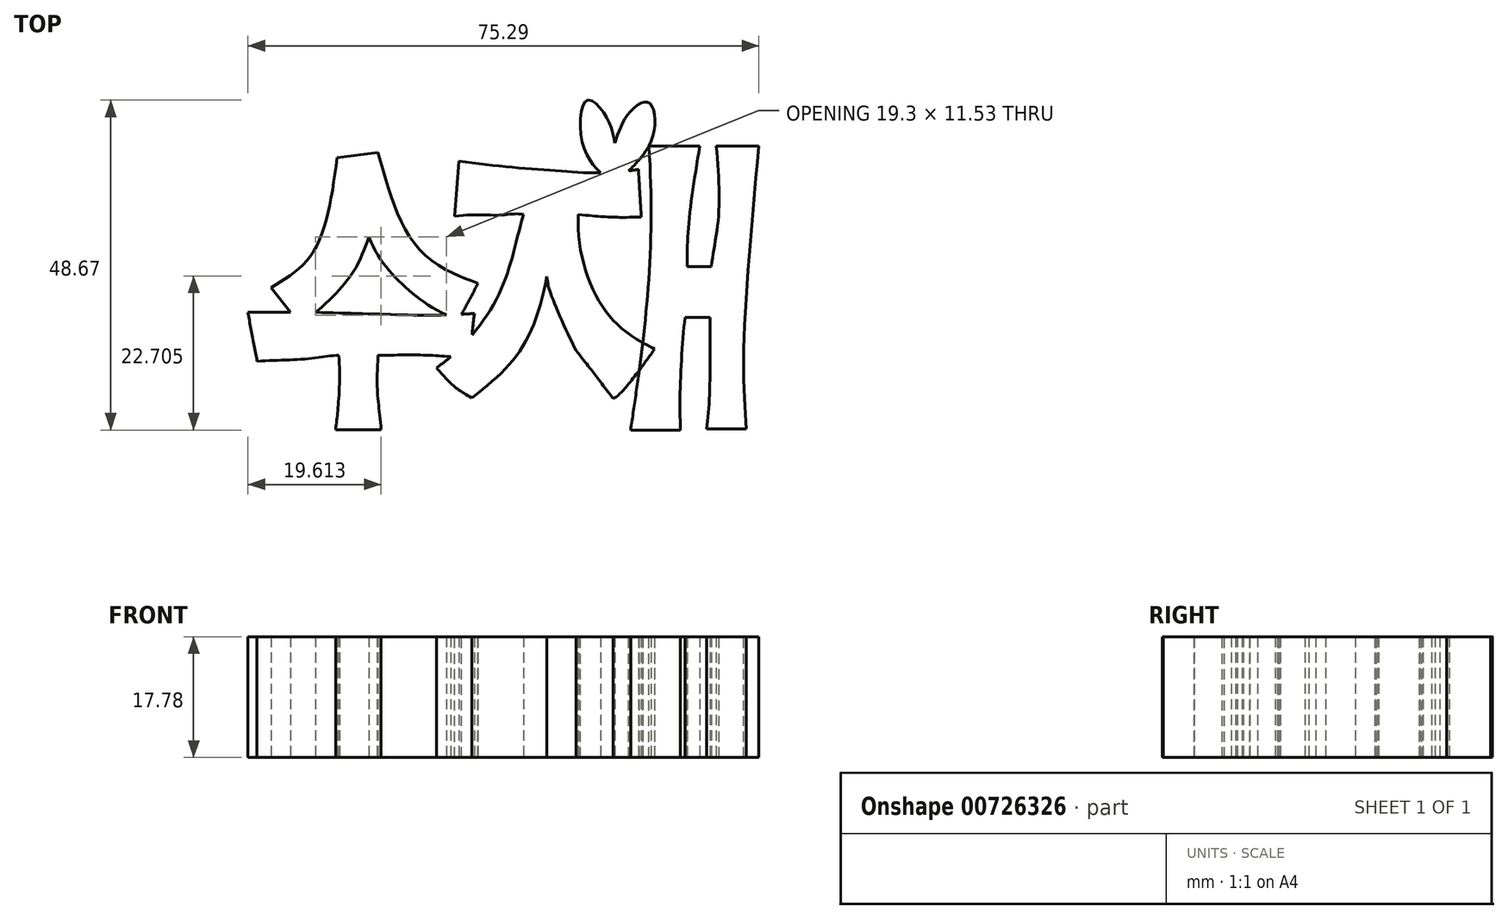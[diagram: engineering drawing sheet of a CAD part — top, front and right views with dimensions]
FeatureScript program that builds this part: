
annotation { "Feature Type Name" : "Feature", "Feature Type Description" : "" }
export const myFeature = defineFeature(function(context is Context, id is Id, definition is map)
    precondition{}
    {
        {
            var Q0;
            Q0=qCreatedBy(makeId("Top.planeOp"),FACE);
            var sketch = newSketch(context, id + "F0", { "sketchPlane" : qUnion([Q0])});
            skFitSpline(sketch, "E0", {"points": [v(2.13, 22.32) * mm, v(16.32, 20.9) * mm, v(28.6, 21.08) * mm], "startDerivative": vector(28.9, -4.5) * mm, "endDerivative": vector(31.91, 5.2) * mm});
            skFitSpline(sketch, "E1", {"points": [v(28.6, 21.08) * mm, v(29.03, 14.04) * mm], "startDerivative": vector(0.6, -9.53) * mm, "endDerivative": vector(0.6, -9.53) * mm});
            skFitSpline(sketch, "E2", {"points": [v(29.03, 14.04) * mm, v(24.64, 14.04) * mm, v(19.76, 14.4) * mm], "startDerivative": vector(-16.39, -0.24) * mm, "endDerivative": vector(-12.71, 1.09) * mm});
            skFitSpline(sketch, "E3", {"points": [v(19.76, 14.4) * mm, v(22.82, 1.62) * mm, v(30.98, -5.4) * mm], "startDerivative": vector(-1.8, -25.53) * mm, "endDerivative": vector(24.7, -11.9) * mm});
            skFitSpline(sketch, "E4", {"points": [v(30.98, -5.4) * mm, v(24.84, -12.63) * mm, v(24.64, -12.17) * mm], "startDerivative": vector(-8.04, -11.72) * mm, "endDerivative": vector(-1.24, 0.54) * mm});
            skFitSpline(sketch, "E5", {"points": [v(24.84, -12.63) * mm, v(19.4, -5.6) * mm], "startDerivative": vector(-7.3, 9.33) * mm, "endDerivative": vector(-7.3, 9.33) * mm});
            skFitSpline(sketch, "E6", {"points": [v(19.4, -5.6) * mm, v(15.4, 3.53) * mm, v(15.1, 5.27) * mm], "startDerivative": vector(-6.57, 12.38) * mm, "endDerivative": vector(-2.12, 12.03) * mm});
            skFitSpline(sketch, "E7", {"points": [v(15.1, 5.27) * mm, v(11.1, -5.75) * mm, v(4.07, -12.63) * mm], "startDerivative": vector(-4.59, -25.5) * mm, "endDerivative": vector(-18.61, -14.97) * mm});
            skFitSpline(sketch, "E8", {"points": [v(2.13, 22.32) * mm, v(1.52, 14.2) * mm], "startDerivative": vector(-0.6, -8.11) * mm, "endDerivative": vector(-0.6, -8.11) * mm});
            skFitSpline(sketch, "E9", {"points": [v(1.52, 14.2) * mm, v(8.32, 14.35) * mm, v(11.66, 14.4) * mm], "startDerivative": vector(14.52, 1.77) * mm, "endDerivative": vector(7.73, -2.03) * mm});
            skFitSpline(sketch, "E10", {"points": [v(11.66, 14.4) * mm, v(8.01, 2.64) * mm, v(-1.16, -8.18) * mm], "startDerivative": vector(-7.44, -24.73) * mm, "endDerivative": vector(-20.98, -14.6) * mm});
            skFitSpline(sketch, "E11", {"points": [v(-1.16, -8.18) * mm, v(4.07, -12.63) * mm], "startDerivative": vector(5.88, -6.7) * mm, "endDerivative": vector(7.72, -4.21) * mm});
            skFitSpline(sketch, "E12", {"points": [v(30.13, 24.54) * mm, v(29.6, -1.15) * mm, v(27.45, -17.36) * mm], "startDerivative": vector(3.69, -50.92) * mm, "endDerivative": vector(-4.55, -30.72) * mm});
            skFitSpline(sketch, "E13", {"points": [v(27.45, -17.36) * mm, v(32.15, -17.36) * mm, v(34.78, -17.36) * mm], "startDerivative": vector(11.12, 0) * mm, "endDerivative": vector(4.43, 0) * mm});
            skFitSpline(sketch, "E14", {"points": [v(30.13, 24.54) * mm, v(35.6, 24.53) * mm, v(37.64, 24.53) * mm], "startDerivative": vector(9.88, 0) * mm, "endDerivative": vector(4.7, 0) * mm});
            skFitSpline(sketch, "E15", {"points": [v(37.64, 24.53) * mm, v(36, 12.98) * mm, v(35.8, 6.73) * mm], "startDerivative": vector(-3.49, -21.54) * mm, "endDerivative": vector(0.02, -13.75) * mm});
            skFitSpline(sketch, "E16", {"points": [v(35.8, 6.73) * mm, v(39.35, 6.73) * mm], "startDerivative": vector(4.66, 0) * mm, "endDerivative": vector(4.66, 0) * mm});
            skFitSpline(sketch, "E17", {"points": [v(39.35, 6.73) * mm, v(40.35, 13.61) * mm, v(40.06, 24.54) * mm], "startDerivative": vector(1.45, 14.36) * mm, "endDerivative": vector(-2.1, 21.05) * mm});
            skFitSpline(sketch, "E18", {"points": [v(40.06, 24.54) * mm, v(46.34, 24.54) * mm], "startDerivative": vector(6.29, 0) * mm, "endDerivative": vector(6.29, 0) * mm});
            skFitSpline(sketch, "E19", {"points": [v(46.34, 24.54) * mm, v(44.11, -5.88) * mm, v(44.52, -17.2) * mm], "startDerivative": vector(-5, -54.56) * mm, "endDerivative": vector(1.95, -24.8) * mm});
            skFitSpline(sketch, "E20", {"points": [v(44.52, -17.2) * mm, v(38.66, -17.2) * mm], "startDerivative": vector(-6.05, 0) * mm, "endDerivative": vector(-6.05, 0) * mm});
            skFitSpline(sketch, "E21", {"points": [v(35.46, -0.74) * mm, v(34.76, -11.05) * mm, v(34.78, -17.36) * mm], "startDerivative": vector(-1.76, -16.32) * mm, "endDerivative": vector(0.3, -8.84) * mm});
            skFitSpline(sketch, "E22", {"points": [v(35.46, -0.74) * mm, v(39.13, -0.74) * mm], "startDerivative": vector(3.75, 0) * mm, "endDerivative": vector(3.75, 0) * mm});
            skFitSpline(sketch, "E23", {"points": [v(39.13, -0.74) * mm, v(39.13, -10.08) * mm, v(38.66, -17.2) * mm], "startDerivative": vector(0.35, -12.35) * mm, "endDerivative": vector(-1.8, -13.24) * mm});
            skFitSpline(sketch, "E24", {"points": [v(-9.78, 23.55) * mm, v(-2.06, 7.75) * mm, v(4.94, 4.26) * mm, v(4.37, 4.26) * mm], "startDerivative": vector(9.05, -33.14) * mm, "endDerivative": vector(-5.8, 0.47) * mm});
            skFitSpline(sketch, "E25", {"points": [v(4.94, 4.26) * mm, v(2.4, -0.45) * mm, v(1.92, -1.05) * mm], "startDerivative": vector(-4.13, -8.05) * mm, "endDerivative": vector(-1.51, -1.6) * mm});
            skFitSpline(sketch, "E26", {"points": [v(1.92, -1.05) * mm, v(-6.18, 4.12) * mm, v(-11.12, 11.11) * mm], "startDerivative": vector(-20.68, 7.63) * mm, "endDerivative": vector(-6.86, 18.33) * mm});
            skFitSpline(sketch, "E27", {"points": [v(-11.12, 11.11) * mm, v(-14.53, 4.46) * mm, v(-21.47, -1.53) * mm], "startDerivative": vector(-8.54, -21.91) * mm, "endDerivative": vector(-10.7, -3.24) * mm});
            skFitSpline(sketch, "E28", {"points": [v(-21.47, -1.53) * mm, v(-25.57, 3.65) * mm], "startDerivative": vector(-4.1, 5.19) * mm, "endDerivative": vector(-4.1, 5.19) * mm});
            skFitSpline(sketch, "E29", {"points": [v(-25.57, 3.65) * mm, v(-19.3, 8.96) * mm, v(-15.8, 22.83) * mm], "startDerivative": vector(16.36, 9.7) * mm, "endDerivative": vector(3.76, 27.81) * mm});
            skFitSpline(sketch, "E30", {"points": [v(-15.8, 22.83) * mm, v(-9.78, 23.55) * mm], "startDerivative": vector(6.03, 0.72) * mm, "endDerivative": vector(6.03, 0.72) * mm});
            skFitSpline(sketch, "E31", {"points": [v(-28.95, 0) * mm, v(-27.62, -7.2) * mm], "startDerivative": vector(0.96, -6.51) * mm, "endDerivative": vector(0.96, -6.51) * mm});
            skFitSpline(sketch, "E32", {"points": [v(-27.62, -7.2) * mm, v(-20.15, -6.84) * mm, v(-15.58, -6.36) * mm], "startDerivative": vector(13.94, 0.8) * mm, "endDerivative": vector(8.7, -0.13) * mm});
            skFitSpline(sketch, "E33", {"points": [v(-15.58, -6.36) * mm, v(-15.69, -14.07) * mm, v(-16.05, -17.32) * mm], "startDerivative": vector(1.33, -13.54) * mm, "endDerivative": vector(-1.2, -8.64) * mm});
            skFitSpline(sketch, "E34", {"points": [v(-16.05, -17.32) * mm, v(-9.34, -17.32) * mm], "startDerivative": vector(6.51, 0) * mm, "endDerivative": vector(6.51, 0) * mm});
            skFitSpline(sketch, "E35", {"points": [v(-9.34, -17.32) * mm, v(-9.9, -11.3) * mm, v(-9.78, -6.36) * mm], "startDerivative": vector(-0.92, 13.01) * mm, "endDerivative": vector(0.48, 10.31) * mm});
            skFitSpline(sketch, "E36", {"points": [v(-9.78, -6.36) * mm, v(-1.94, -6.36) * mm, v(4.57, -6.96) * mm], "startDerivative": vector(15.35, 0.33) * mm, "endDerivative": vector(13.32, -1.56) * mm});
            skFitSpline(sketch, "E37", {"points": [v(4.57, -6.96) * mm, v(4.1, -5.66) * mm, v(4.43, -0.15) * mm], "startDerivative": vector(-1.4, 7.86) * mm, "endDerivative": vector(1.14, 8.06) * mm});
            skFitSpline(sketch, "E38", {"points": [v(4.43, -0.15) * mm, v(-11.34, -0.2) * mm, v(-28.95, 0) * mm], "startDerivative": vector(-31.92, -2.84) * mm, "endDerivative": vector(-34.15, -0.56) * mm});
            skLineSegment(sketch, "E39", {"start": v(-9.34, -17.32) * mm, "end": v(27.45, -17.32) * mm});
            skFitSpline(sketch, "E40", {"points": [v(23, 20.56) * mm, v(20.28, 25.23) * mm, v(21, 31.25) * mm, v(23.72, 29.1) * mm, v(25.15, 24.95) * mm], "startDerivative": vector(-12.81, 13.62) * mm, "endDerivative": vector(3.61, -17.19) * mm});
            skFitSpline(sketch, "E41", {"points": [v(25.15, 24.95) * mm, v(27.02, 29.1) * mm, v(30.03, 30.97) * mm, v(30.88, 26.53) * mm, v(27.16, 20.87) * mm], "startDerivative": vector(5.35, 17.44) * mm, "endDerivative": vector(-16.46, -16.47) * mm});
            skSolve(sketch);
        }
        {
            var Q0;
            {var subQ5=sQuery(id+"F0.wireOp",EDGE,"E13");Q0=makeQuery(id+"F0.imprint","IMPRINT",FACE,{"disambiguationData":[TD([[makeQuery(id+"F0.imprint","IMPRINT",EDGE,{"derivedFrom":subQ5}),1.0]])]});}
            var Q1;
            {var subQ0=sQuery(id+"F0.wireOp",EDGE,"E40");Q1=makeQuery(id+"F0.imprint","IMPRINT",FACE,{"disambiguationData":[TD([[makeQuery(id+"F0.imprint","IMPRINT",EDGE,{"derivedFrom":subQ0}),-1.0]])]});}
            var Q2;
            {var subQ0=sQuery(id+"F0.wireOp",EDGE,"E7");var subQ1=sQuery(id+"F0.wireOp",EDGE,"E6");var subQ2=makeQuery(id+"F0.imprint","INTERSECT",VERTEX,{"disambiguationData":[OD(0.0)],"derivedFrom":[subQ1,subQ0]});Q2=makeQuery(id+"F0.imprint","IMPRINT",FACE,{"disambiguationData":[TD([[makeQuery(id+"F0.imprint","IMPRINT",EDGE,{"disambiguationData":[TD([[subQ2,1.0]])],"derivedFrom":subQ1}),1.0]])]});}
            var Q3;
            {var subQ19=sQuery(id+"F0.wireOp",EDGE,"E1");Q3=makeQuery(id+"F0.imprint","IMPRINT",FACE,{"disambiguationData":[TD([[makeQuery(id+"F0.imprint","IMPRINT",EDGE,{"derivedFrom":subQ19}),-1.0]])]});}
            var Q4;
            {var subQ13=sQuery(id+"F0.wireOp",EDGE,"E29");Q4=makeQuery(id+"F0.imprint","IMPRINT",FACE,{"disambiguationData":[TD([[makeQuery(id+"F0.imprint","IMPRINT",EDGE,{"derivedFrom":subQ13}),-1.0]])]});}
            var Q5;
            {var subQ0=sQuery(id+"F0.wireOp",EDGE,"E28");var subQ1=sQuery(id+"F0.wireOp",EDGE,"E27");var subQ2=makeQuery(id+"F0.imprint","INTERSECT",VERTEX,{"derivedFrom":[subQ1,subQ0]});Q5=makeQuery(id+"F0.imprint","IMPRINT",FACE,{"disambiguationData":[TD([[makeQuery(id+"F0.imprint","IMPRINT",EDGE,{"disambiguationData":[TD([[subQ2,1.0]])],"derivedFrom":subQ1}),-1.0]])]});}
            var Q6;
            {var subQ0=sQuery(id+"F0.wireOp",EDGE,"E26");var subQ1=sQuery(id+"F0.wireOp",EDGE,"E25");var subQ2=makeQuery(id+"F0.imprint","INTERSECT",VERTEX,{"derivedFrom":[subQ1,subQ0]});Q6=makeQuery(id+"F0.imprint","IMPRINT",FACE,{"disambiguationData":[TD([[makeQuery(id+"F0.imprint","IMPRINT",EDGE,{"disambiguationData":[TD([[subQ2,1.0]])],"derivedFrom":subQ1}),-1.0]])]});}
            var Q7;
            {var subQ1=sQuery(id+"F0.wireOp",EDGE,"E31");Q7=makeQuery(id+"F0.imprint","IMPRINT",FACE,{"disambiguationData":[TD([[makeQuery(id+"F0.imprint","IMPRINT",EDGE,{"derivedFrom":subQ1}),1.0]])]});}
            var Q8;
            {var subQ0=sQuery(id+"F0.wireOp",EDGE,"E37");var subQ1=sQuery(id+"F0.wireOp",EDGE,"E10");var subQ2=makeQuery(id+"F0.imprint","INTERSECT",VERTEX,{"derivedFrom":[subQ1,subQ0]});Q8=makeQuery(id+"F0.imprint","IMPRINT",FACE,{"disambiguationData":[TD([[makeQuery(id+"F0.imprint","IMPRINT",EDGE,{"disambiguationData":[TD([[subQ2,-1.0]])],"derivedFrom":subQ1}),1.0]])]});}
            extrude(context, id + "F1", {"entities" : qUnion([Q0, Q1, Q2, Q3, Q4, Q5, Q6, Q7, Q8]), "depth" : 17.78 * mm, "offsetDistance" : 25.4 * mm});
        }
        {
            var Q0;
            {var subQ0=sQuery(id+"F0.wireOp",EDGE,"E4");var subQ1=sQuery(id+"F0.wireOp",EDGE,"E3");var subQ2=makeQuery(id+"F0.imprint","INTERSECT",VERTEX,{"derivedFrom":[subQ1,subQ0]});Q0=makeQuery(id+"F0.imprint","IMPRINT",FACE,{"disambiguationData":[TD([[makeQuery(id+"F0.imprint","IMPRINT",EDGE,{"disambiguationData":[TD([[subQ2,1.0]])],"derivedFrom":subQ1}),-1.0]])]});}
            extrude(context, id + "F2", {"entities" : qUnion([Q0]), "depth" : 17.78 * mm, "offsetDistance" : 25.4 * mm});
        }
    });
